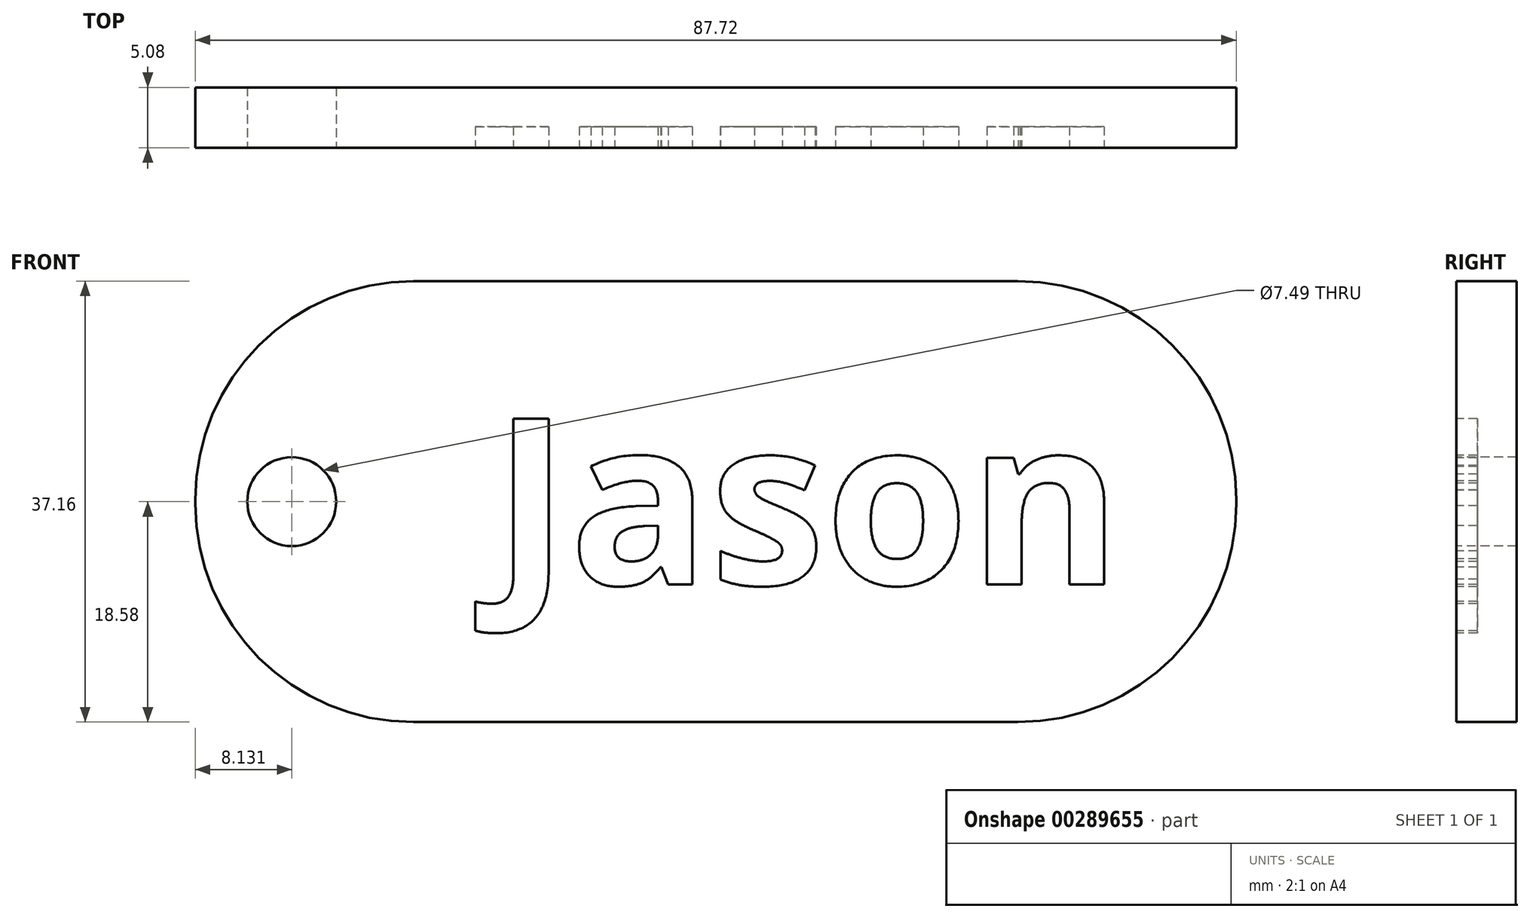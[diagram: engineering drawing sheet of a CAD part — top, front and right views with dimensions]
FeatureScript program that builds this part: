
annotation { "Feature Type Name" : "Feature", "Feature Type Description" : "" }
export const myFeature = defineFeature(function(context is Context, id is Id, definition is map)
    precondition{}
    {
        {
            var Q0;
            Q0=qCreatedBy(makeId("Front.planeOp"),FACE);
            var sketch = newSketch(context, id + "F0", { "sketchPlane" : qUnion([Q0])});
            skLineSegment(sketch, "E0.bottom", {"start": v(43.86, -18.58) * mm, "end": v(-43.86, -18.58) * mm});
            skLineSegment(sketch, "E0.top", {"start": v(43.86, 18.58) * mm, "end": v(-43.86, 18.58) * mm});
            skLineSegment(sketch, "E0.left", {"start": v(43.86, -18.58) * mm, "end": v(43.86, 18.58) * mm});
            skLineSegment(sketch, "E0.right", {"start": v(-43.86, -18.58) * mm, "end": v(-43.86, 18.58) * mm});
            skPoint(sketch, "E0.middle", {"position": v(0, 0) * mm});
            skSolve(sketch);
        }
        {
            var Q0;
            Q0 = qSketchRegion(id + "F0", true);
            extrude(context, id + "F1", {"entities" : qUnion([Q0]), "depth" : 5.08 * mm});
        }
        {
            var Q0;
            Q0=makeQuery(id+"F1.opExtrude","SWEPT_EDGE",EDGE,{"disambiguationData":[OSD([sQuery(id+"F0.wireOp",EDGE,"E0.top"),sQuery(id+"F0.wireOp",EDGE,"E0.right")])]});
            var Q1;
            Q1=makeQuery(id+"F1.opExtrude","SWEPT_EDGE",EDGE,{"disambiguationData":[OSD([sQuery(id+"F0.wireOp",EDGE,"E0.top"),sQuery(id+"F0.wireOp",EDGE,"E0.left")])]});
            var Q2;
            Q2=makeQuery(id+"F1.opExtrude","SWEPT_EDGE",EDGE,{"disambiguationData":[OSD([sQuery(id+"F0.wireOp",EDGE,"E0.bottom"),sQuery(id+"F0.wireOp",EDGE,"E0.left")])]});
            var Q3;
            Q3=makeQuery(id+"F1.opExtrude","SWEPT_EDGE",EDGE,{"disambiguationData":[OSD([sQuery(id+"F0.wireOp",EDGE,"E0.bottom"),sQuery(id+"F0.wireOp",EDGE,"E0.right")])]});
            fillet(context, id + "F2", {"entities" : qUnion([Q0, Q1, Q2, Q3]), "radius" : 18.4 * mm, "tangentPropagation" : true, "allowEdgeOverflow" : false});
        }
        {
            var Q0;
            Q0=makeQuery(id+"F1.opExtrude","CAP_FACE",FACE,{"disambiguationData":[OSD([sQuery(id+"F0.wireOp",EDGE,"E0.bottom"),sQuery(id+"F0.wireOp",EDGE,"E0.top"),sQuery(id+"F0.wireOp",EDGE,"E0.left"),sQuery(id+"F0.wireOp",EDGE,"E0.right")])],"isStart":false});
            var sketch = newSketch(context, id + "F3", { "sketchPlane" : qUnion([Q0])});
            skCircle(sketch, "E1", {"center": v(-35.73, 0) * mm, "radius": 3.75 * mm});
            skSolve(sketch);
        }
        {
            var Q0;
            Q0 = qSketchRegion(id + "F3", true);
            var Q1;
            Q1=makeQuery(id+"F1.opExtrude","CAP_FACE",FACE,{"disambiguationData":[OSD([sQuery(id+"F0.wireOp",EDGE,"E0.bottom"),sQuery(id+"F0.wireOp",EDGE,"E0.top"),sQuery(id+"F0.wireOp",EDGE,"E0.left"),sQuery(id+"F0.wireOp",EDGE,"E0.right")])],"isStart":true});
            extrude(context, id + "F4", {"entities" : qUnion([Q0]), "operationType" : NewBodyOperationType.REMOVE, "endBound" : BoundingType.UP_TO_SURFACE, "oppositeDirection" : true, "endBoundEntityFace" : qUnion([Q1]), "depth" : 25.4 * mm});
        }
        {
            var Q0;
            Q0=makeQuery(id+"F1.opExtrude","CAP_FACE",FACE,{"disambiguationData":[OSD([sQuery(id+"F0.wireOp",EDGE,"E0.bottom"),sQuery(id+"F0.wireOp",EDGE,"E0.top"),sQuery(id+"F0.wireOp",EDGE,"E0.left"),sQuery(id+"F0.wireOp",EDGE,"E0.right")])],"isStart":false});
            var sketch = newSketch(context, id + "F5", { "sketchPlane" : qUnion([Q0])});
            skText(sketch, "E2", { "text": "Jason", "fontName": "OpenSans-Bold.ttf"});
            const initialGuessF5  = {"E2": [-0.01881, -0.00698, 1, 0, 0.01409]};
            skSetInitialGuess(sketch, initialGuessF5);
            skSolve(sketch);
        }
        {
            var Q0;
            Q0 = qSketchRegion(id + "F5", true);
            extrude(context, id + "F6", {"entities" : qUnion([Q0]), "operationType" : NewBodyOperationType.REMOVE, "oppositeDirection" : true, "depth" : 1.78 * mm});
        }
    });
